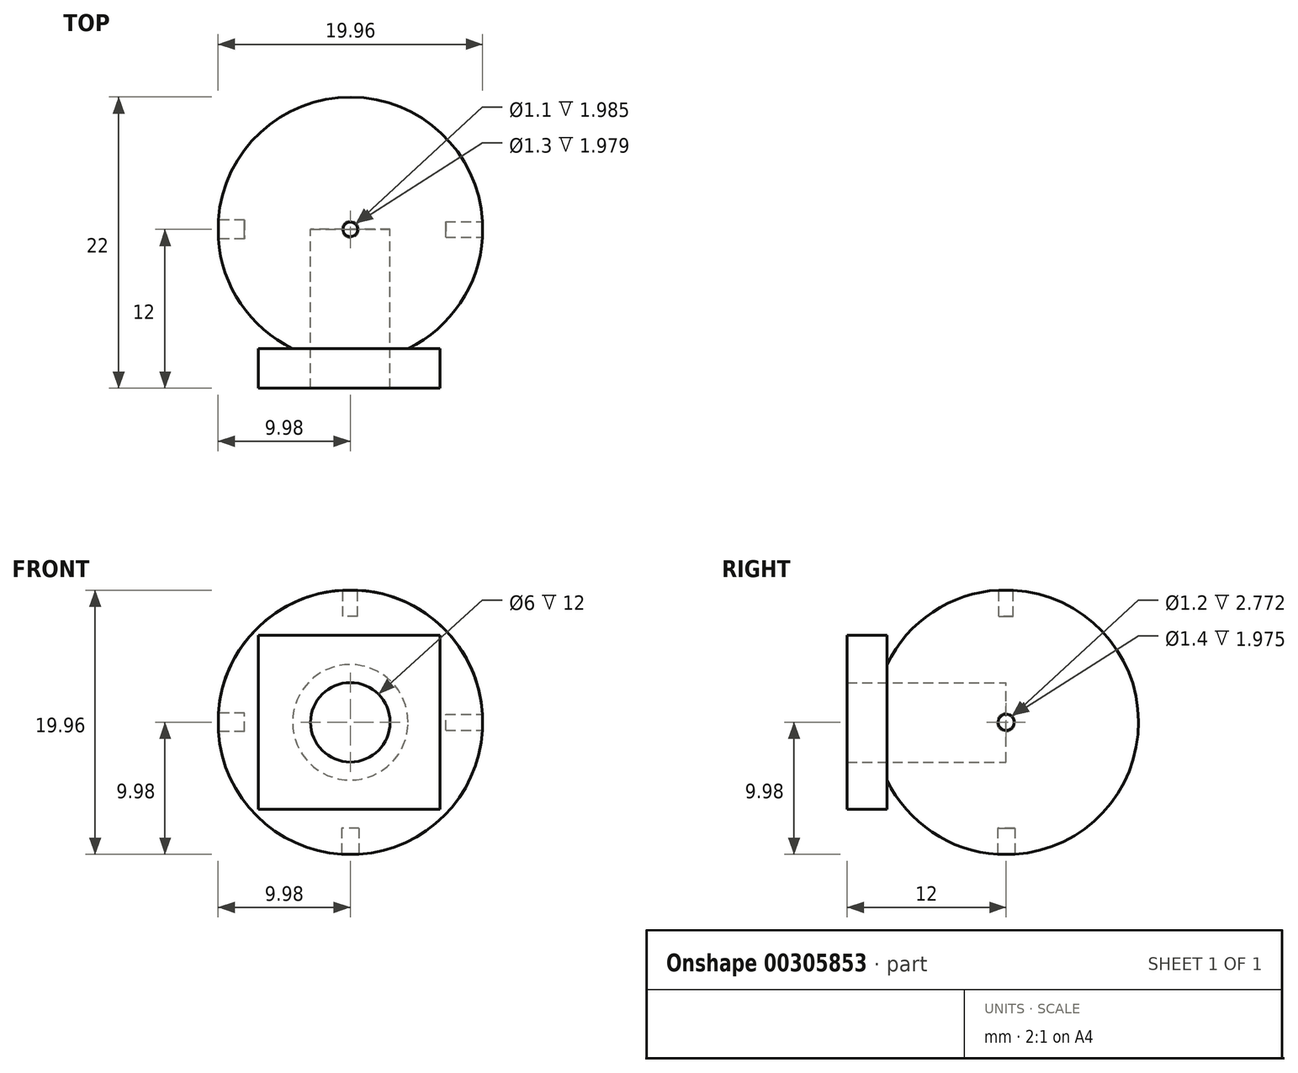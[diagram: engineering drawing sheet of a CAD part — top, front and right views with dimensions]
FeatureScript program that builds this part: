
annotation { "Feature Type Name" : "Feature", "Feature Type Description" : "" }
export const myFeature = defineFeature(function(context is Context, id is Id, definition is map)
    precondition{}
    {
        {
            var Q0;
            Q0=qCreatedBy(makeId("Front.planeOp"),FACE);
            var sketch = newSketch(context, id + "F0", { "sketchPlane" : qUnion([Q0])});
            skPoint(sketch, "E0.endSnap0", {"position": v(0, -12.5) * mm});
            skArc(sketch, "E1", {"start": v(-10, 0) * mm, "mid": v(0, -10) * mm, "end": v(10, 0) * mm});
            skLineSegment(sketch, "E2", {"start": v(-10, 0) * mm, "end": v(10, 0) * mm});
            skSolve(sketch);
        }
        {
            var Q0;
            Q0=makeQuery(id+"F0.imprint","IMPRINT",FACE,{"disambiguationData":[TD([[makeQuery(id+"F0.imprint","IMPRINT",EDGE,{"derivedFrom":sQuery(id+"F0.wireOp",EDGE,"E1")}),1.0]])]});
            var Q1;
            Q1=sQuery(id+"F0.wireOp",EDGE,"E2");
            revolve(context, id + "F1", {"entities" : qUnion([Q0]), "axis" : qUnion([Q1]), "revolveType" : RevolveType.FULL});
        }
        {
            var Q0;
            Q0=qCreatedBy(makeId("Front.planeOp"),FACE);
            var sketch = newSketch(context, id + "F2", { "sketchPlane" : qUnion([Q0])});
            skCircle(sketch, "E3", {"center": v(0, 0) * mm, "radius": 3 * mm});
            skSolve(sketch);
        }
        {
            var Q0;
            Q0=qCreatedBy(makeId("Right.planeOp"),FACE);
            cPlane(context, id + "F3", {"entities" : qUnion([Q0]), "cplaneType" : CPlaneType.OFFSET, "offset" : 10 * mm, "width" : 150 * mm, "height" : 150 * mm});
        }
        {
            var Q0;
            Q0=qCreatedBy(makeId("Top.planeOp"),FACE);
            cPlane(context, id + "F4", {"entities" : qUnion([Q0]), "cplaneType" : CPlaneType.OFFSET, "offset" : 10 * mm, "width" : 150 * mm, "height" : 150 * mm});
        }
        {
            var Q0;
            Q0=qCreatedBy(makeId("Top.planeOp"),FACE);
            cPlane(context, id + "F5", {"entities" : qUnion([Q0]), "cplaneType" : CPlaneType.OFFSET, "offset" : 10 * mm, "oppositeDirection" : true, "width" : 150 * mm, "height" : 150 * mm});
        }
        {
            var Q0;
            Q0=qCreatedBy(makeId("Right.planeOp"),FACE);
            cPlane(context, id + "F6", {"entities" : qUnion([Q0]), "cplaneType" : CPlaneType.OFFSET, "offset" : 10 * mm, "oppositeDirection" : true, "width" : 150 * mm, "height" : 150 * mm});
        }
        {
            var Q0;
            Q0=qCreatedBy(id+"F3.planeOp",FACE);
            var sketch = newSketch(context, id + "F7", { "sketchPlane" : qUnion([Q0])});
            skCircle(sketch, "E4", {"center": v(0, 0) * mm, "radius": 0.6 * mm});
            skSolve(sketch);
        }
        {
            var Q0;
            Q0=qCreatedBy(id+"F4.planeOp",FACE);
            var sketch = newSketch(context, id + "F8", { "sketchPlane" : qUnion([Q0])});
            skCircle(sketch, "E5", {"center": v(0, 0) * mm, "radius": 0.55 * mm});
            skSolve(sketch);
        }
        {
            var Q0;
            Q0=qCreatedBy(id+"F5.planeOp",FACE);
            var sketch = newSketch(context, id + "F9", { "sketchPlane" : qUnion([Q0])});
            skCircle(sketch, "E6", {"center": v(0, 0) * mm, "radius": 0.65 * mm});
            skSolve(sketch);
        }
        {
            var Q0;
            Q0=qCreatedBy(id+"F6.planeOp",FACE);
            var sketch = newSketch(context, id + "F10", { "sketchPlane" : qUnion([Q0])});
            skCircle(sketch, "E7", {"center": v(0, 0) * mm, "radius": 0.7 * mm});
            skSolve(sketch);
        }
        {
            var Q0;
            Q0=qSketchRegion(id+"F7",true);
            extrude(context, id + "F11", {"entities" : qUnion([Q0]), "operationType" : NewBodyOperationType.REMOVE, "endBound" : BoundingType.SYMMETRIC, "oppositeDirection" : true, "depth" : 5.58 * mm});
        }
        {
            var Q0;
            Q0=qSketchRegion(id+"F8",true);
            extrude(context, id + "F12", {"entities" : qUnion([Q0]), "operationType" : NewBodyOperationType.REMOVE, "oppositeDirection" : true, "depth" : 2 * mm});
        }
        {
            var Q0;
            Q0=qSketchRegion(id+"F9",true);
            extrude(context, id + "F13", {"entities" : qUnion([Q0]), "operationType" : NewBodyOperationType.REMOVE, "depth" : 2 * mm});
        }
        {
            var Q0;
            Q0=qSketchRegion(id+"F10",true);
            extrude(context, id + "F14", {"entities" : qUnion([Q0]), "operationType" : NewBodyOperationType.REMOVE, "depth" : 2 * mm});
        }
        {
            var Q0;
            Q0=qCreatedBy(makeId("Front.planeOp"),FACE);
            cPlane(context, id + "F15", {"entities" : qUnion([Q0]), "cplaneType" : CPlaneType.OFFSET, "offset" : 9 * mm, "width" : 150 * mm, "height" : 150 * mm});
        }
        {
            var Q0;
            Q0=qCreatedBy(id+"F15.planeOp",FACE);
            var sketch = newSketch(context, id + "F16", { "sketchPlane" : qUnion([Q0])});
            skLineSegment(sketch, "E8.bottom", {"start": v(6.78, 6.58) * mm, "end": v(-6.96, 6.58) * mm});
            skLineSegment(sketch, "E8.top", {"start": v(6.78, -6.58) * mm, "end": v(-6.96, -6.58) * mm});
            skLineSegment(sketch, "E8.left", {"start": v(6.78, 6.58) * mm, "end": v(6.78, -6.58) * mm});
            skLineSegment(sketch, "E8.right", {"start": v(-6.96, 6.58) * mm, "end": v(-6.96, -6.58) * mm});
            skSolve(sketch);
        }
        {
            var Q0;
            Q0 = qSketchRegion(id + "F16", true);
            extrude(context, id + "F17", {"entities" : qUnion([Q0]), "operationType" : NewBodyOperationType.ADD, "depth" : 3 * mm});
        }
        {
            var Q0;
            Q0=qSketchRegion(id+"F2",true);
            var Q1;
            Q1=sQuery(id+"F2.wireOp",EDGE,"E3");
            extrude(context, id + "F18", {"entities" : qUnion([Q0]), "operationType" : NewBodyOperationType.REMOVE, "surfaceEntities" : qUnion([Q1]), "endBound" : BoundingType.THROUGH_ALL, "depth" : 50 * mm});
        }
    });
